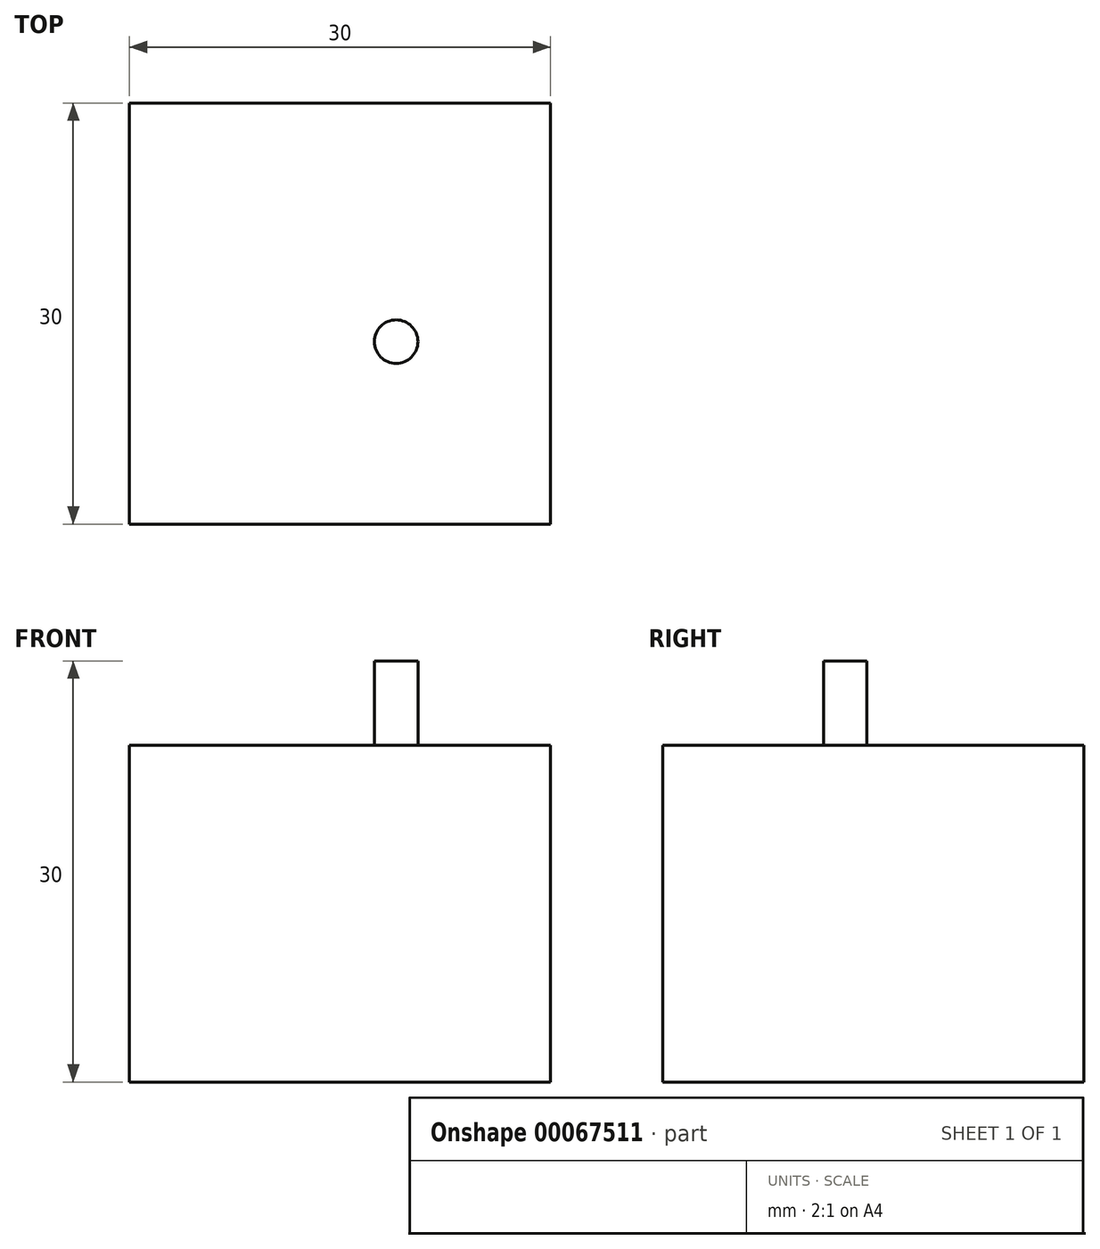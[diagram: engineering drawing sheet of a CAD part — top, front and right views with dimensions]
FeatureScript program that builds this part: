
annotation { "Feature Type Name" : "Feature", "Feature Type Description" : "" }
export const myFeature = defineFeature(function(context is Context, id is Id, definition is map)
    precondition{}
    {
        {
            var Q0;
            Q0=qCreatedBy(makeId("Top.planeOp"),FACE);
            var sketch = newSketch(context, id + "F0", { "sketchPlane" : qUnion([Q0])});
            skLineSegment(sketch, "E0.rect.bottom", {"start": v(15, 15) * mm, "end": v(-15, 15) * mm});
            skLineSegment(sketch, "E0.rect.top", {"start": v(15, -15) * mm, "end": v(-15, -15) * mm});
            skLineSegment(sketch, "E0.rect.left", {"start": v(15, 15) * mm, "end": v(15, -15) * mm});
            skLineSegment(sketch, "E0.rect.right", {"start": v(-15, 15) * mm, "end": v(-15, -15) * mm});
            skPoint(sketch, "E0.rect.middle", {"position": v(0, 0) * mm});
            skSolve(sketch);
        }
        {
            var Q0;
            Q0 = qSketchRegion(id + "F0", true);
            extrude(context, id + "F1", {"entities" : qUnion([Q0]), "depth" : 30 * mm});
        }
        {
            var Q0;
            Q0=makeQuery(id+"F1.opExtrude","CAP_FACE",FACE,{"disambiguationData":[OSD([sQuery(id+"F0.wireOp",EDGE,"E0.rect.bottom"),sQuery(id+"F0.wireOp",EDGE,"E0.rect.top"),sQuery(id+"F0.wireOp",EDGE,"E0.rect.left"),sQuery(id+"F0.wireOp",EDGE,"E0.rect.right")])],"isStart":false});
            var sketch = newSketch(context, id + "F2", { "sketchPlane" : qUnion([Q0])});
            skLineSegment(sketch, "E1", {"start": v(0, 0) * mm, "end": v(0, 0) * mm});
            skCircle(sketch, "E2", {"center": v(-4, -2) * mm, "radius": 1.55 * mm});
            skCircle(sketch, "E3.MirrorC", {"center": v(4, -2) * mm, "radius": 1.55 * mm});
            skSolve(sketch);
        }
        {
            var Q0;
            Q0=makeQuery(id+"F2.imprint","IMPRINT",FACE,{"disambiguationData":[TD([[makeQuery(id+"F2.imprint","IMPRINT",EDGE,{"derivedFrom":sQuery(id+"F2.wireOp",EDGE,"6ea1613d-109e-40ce-a016-63cb34eefbe3")}),1.0]])]});
            var Q1;
            Q1=makeQuery(id+"F2.imprint","IMPRINT",FACE,{"disambiguationData":[TD([[makeQuery(id+"F2.imprint","IMPRINT",EDGE,{"derivedFrom":sQuery(id+"F2.wireOp",EDGE,"ea25e9c1-0f7d-4291-a163-112e664b112f0.MirrorC")}),-1.0]])]});
            var Q2;
            Q2=makeQuery(id+"F2.imprint","IMPRINT",FACE,{"disambiguationData":[TD([[makeQuery(id+"F2.imprint","IMPRINT",EDGE,{"derivedFrom":sQuery(id+"F2.wireOp",EDGE,"E3.MirrorC")}),-1.0]])]});
            var Q3;
            Q3=makeQuery(id+"F2.imprint","IMPRINT",FACE,{"disambiguationData":[TD([[makeQuery(id+"F2.imprint","IMPRINT",EDGE,{"derivedFrom":sQuery(id+"F2.wireOp",EDGE,"E2")}),1.0]])]});
            extrude(context, id + "F3", {"entities" : qUnion([Q0, Q1, Q2, Q3]), "operationType" : NewBodyOperationType.REMOVE, "oppositeDirection" : true, "depth" : 6 * mm});
        }
    });
